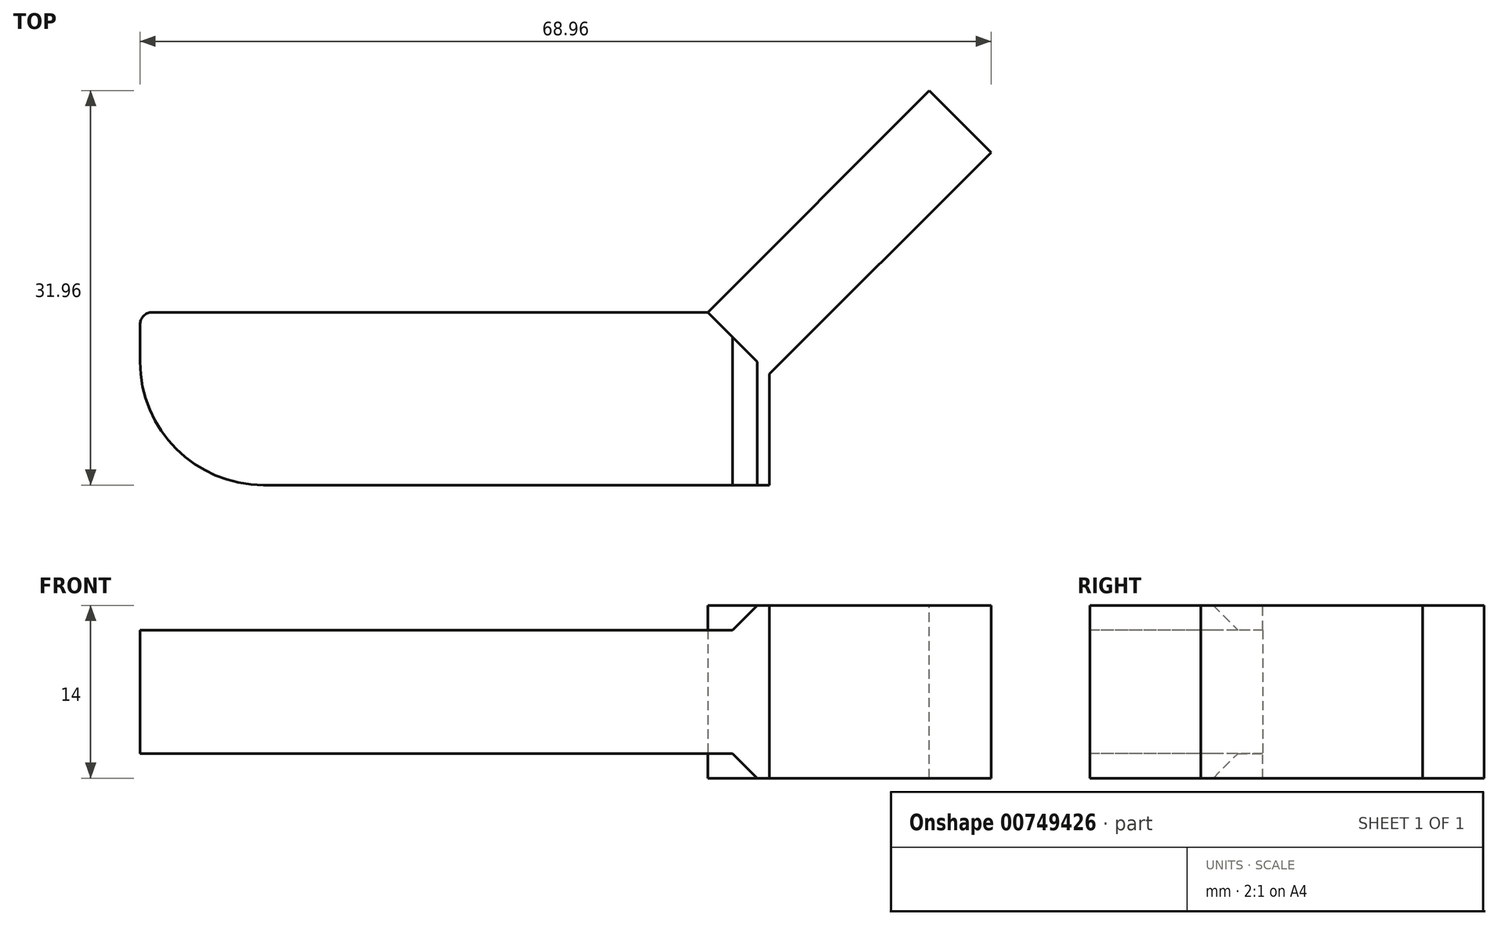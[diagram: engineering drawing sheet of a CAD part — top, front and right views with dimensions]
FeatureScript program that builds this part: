
annotation { "Feature Type Name" : "Feature", "Feature Type Description" : "" }
export const myFeature = defineFeature(function(context is Context, id is Id, definition is map)
    precondition{}
    {
        {
            var Q0;
            Q0=qCreatedBy(makeId("Top.planeOp"),FACE);
            var sketch = newSketch(context, id + "F0", { "sketchPlane" : qUnion([Q0])});
            skLineSegment(sketch, "E0.bottom", {"start": v(-25, 7) * mm, "end": v(25, 7) * mm});
            skLineSegment(sketch, "E0.top", {"start": v(-25, -7) * mm, "end": v(25, -7) * mm});
            skLineSegment(sketch, "E0.left", {"start": v(-25, 7) * mm, "end": v(-25, -7) * mm});
            skLineSegment(sketch, "E0.right", {"start": v(25, 7) * mm, "end": v(25, -7) * mm});
            skPoint(sketch, "E0.middle", {"position": v(0, 0) * mm});
            skSolve(sketch);
        }
        {
            var Q0;
            Q0 = qSketchRegion(id + "F0", true);
            extrude(context, id + "F1", {"entities" : qUnion([Q0]), "depth" : 5 * mm, "offsetDistance" : 25.4 * mm, "hasSecondDirection" : true, "secondDirectionOppositeDirection" : true, "secondDirectionDepth" : 5 * mm});
        }
        {
            var Q0;
            Q0=makeQuery(id+"F1.opExtrude","SWEPT_EDGE",EDGE,{"disambiguationData":[OSD([sQuery(id+"F0.wireOp",EDGE,"E0.bottom"),sQuery(id+"F0.wireOp",EDGE,"E0.left")])]});
            fillet(context, id + "F2", {"entities" : qUnion([Q0]), "radius" : 1 * mm, "tangentPropagation" : true, "allowEdgeOverflow" : false});
        }
        {
            var Q0;
            Q0=makeQuery(id+"F1.opExtrude","SWEPT_EDGE",EDGE,{"disambiguationData":[OSD([sQuery(id+"F0.wireOp",EDGE,"E0.top"),sQuery(id+"F0.wireOp",EDGE,"E0.left")])]});
            fillet(context, id + "F3", {"entities" : qUnion([Q0]), "radius" : 10 * mm, "tangentPropagation" : true, "allowEdgeOverflow" : false});
        }
        {
            var Q0;
            Q0=makeQuery(id+"F1.opExtrude","SWEPT_FACE",FACE,{"disambiguationData":[OSD([sQuery(id+"F0.wireOp",EDGE,"E0.right")])]});
            var sketch = newSketch(context, id + "F4", { "sketchPlane" : qUnion([Q0])});
            skLineSegment(sketch, "E1.bottom", {"start": v(7, 7) * mm, "end": v(-7, 7) * mm});
            skLineSegment(sketch, "E1.top", {"start": v(7, -7) * mm, "end": v(-7, -7) * mm});
            skLineSegment(sketch, "E1.left", {"start": v(7, 7) * mm, "end": v(7, -7) * mm});
            skLineSegment(sketch, "E1.right", {"start": v(-7, 7) * mm, "end": v(-7, -7) * mm});
            skPoint(sketch, "E1.middle", {"position": v(0, 0) * mm});
            skSolve(sketch);
        }
        {
            var Q0;
            Q0 = qSketchRegion(id + "F4", true);
            extrude(context, id + "F5", {"entities" : qUnion([Q0]), "operationType" : NewBodyOperationType.ADD, "depth" : 1 * mm, "offsetDistance" : 25.4 * mm, "hasSecondDirection" : true, "secondDirectionOppositeDirection" : true, "secondDirectionDepth" : 5 * mm});
        }
        {
            var Q0;
            Q0=makeQuery(id+"F5.opExtrude","CAP_EDGE",EDGE,{"disambiguationData":[OSD([sQuery(id+"F4.wireOp",EDGE,"E1.bottom")])],"isStart":true});
            var Q1;
            Q1=makeQuery(id+"F5.opExtrude","CAP_EDGE",EDGE,{"disambiguationData":[OSD([sQuery(id+"F4.wireOp",EDGE,"E1.top")])],"isStart":true});
            chamfer(context, id + "F6", {"entities" : qUnion([Q0, Q1]), "width" : 5 * mm, "tangentPropagation" : true});
        }
        {
            var Q0;
            Q0=makeQuery(id+"F5.opExtrude","CAP_EDGE",EDGE,{"disambiguationData":[OSD([sQuery(id+"F4.wireOp",EDGE,"E1.left")])],"isStart":false});
            chamfer(context, id + "F7", {"entities" : qUnion([Q0]), "width" : 5 * mm, "tangentPropagation" : true});
        }
        {
            var Q0;
            Q0=makeQuery(id+"F7.opChamfer","BLEND_FACE",FACE,{"disambiguationData":[OSD([sQuery(id+"F4.wireOp",EDGE,"E1.left")])]});
            var sketch = newSketch(context, id + "F8", { "sketchPlane" : qUnion([Q0])});
            skLineSegment(sketch, "E2", {"start": v(-16.97, 7) * mm, "end": v(-16.97, -7) * mm});
            skLineSegment(sketch, "E3", {"start": v(-16.97, -7) * mm, "end": v(-9.9, -7) * mm});
            skLineSegment(sketch, "E4", {"start": v(-9.9, -7) * mm, "end": v(-9.9, 7) * mm});
            skLineSegment(sketch, "E5", {"start": v(-9.9, 7) * mm, "end": v(-16.97, 7) * mm});
            skSolve(sketch);
        }
        {
            var Q0;
            Q0 = qSketchRegion(id + "F8", true);
            extrude(context, id + "F9", {"entities" : qUnion([Q0]), "operationType" : NewBodyOperationType.ADD, "depth" : 25.4 * mm, "offsetDistance" : 25.4 * mm});
        }
    });
